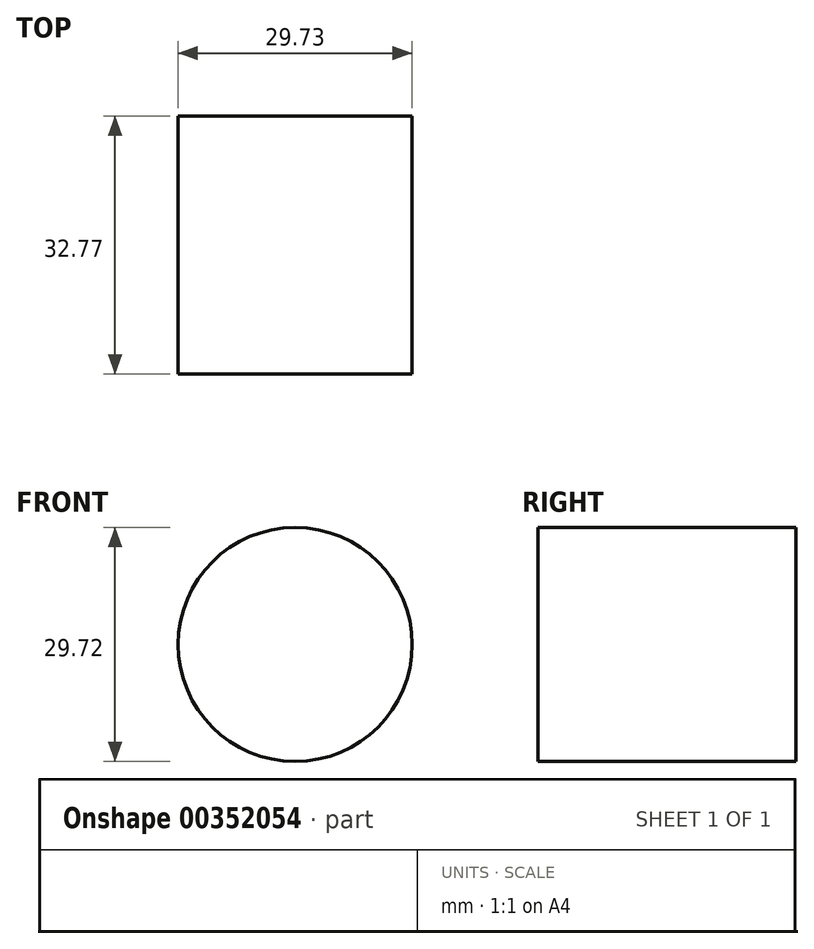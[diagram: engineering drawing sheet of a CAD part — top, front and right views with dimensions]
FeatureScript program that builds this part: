
annotation { "Feature Type Name" : "Feature", "Feature Type Description" : "" }
export const myFeature = defineFeature(function(context is Context, id is Id, definition is map)
    precondition{}
    {
        {
            var Q0;
            Q0=qCreatedBy(makeId("Front.planeOp"),FACE);
            var sketch = newSketch(context, id + "F0", { "sketchPlane" : qUnion([Q0])});
            skCircle(sketch, "E0", {"center": v(-19.69, 21.19) * mm, "radius": 14.86 * mm});
            skSolve(sketch);
        }
        {
            var Q0;
            Q0=makeQuery(id+"F0.imprint","IMPRINT",FACE,{"disambiguationData":[TD([[makeQuery(id+"F0.imprint","IMPRINT",EDGE,{"derivedFrom":sQuery(id+"F0.wireOp",EDGE,"E0")}),1.0]])]});
            extrude(context, id + "F1", {"entities" : qUnion([Q0]), "depth" : 32.77 * mm});
        }
    });
